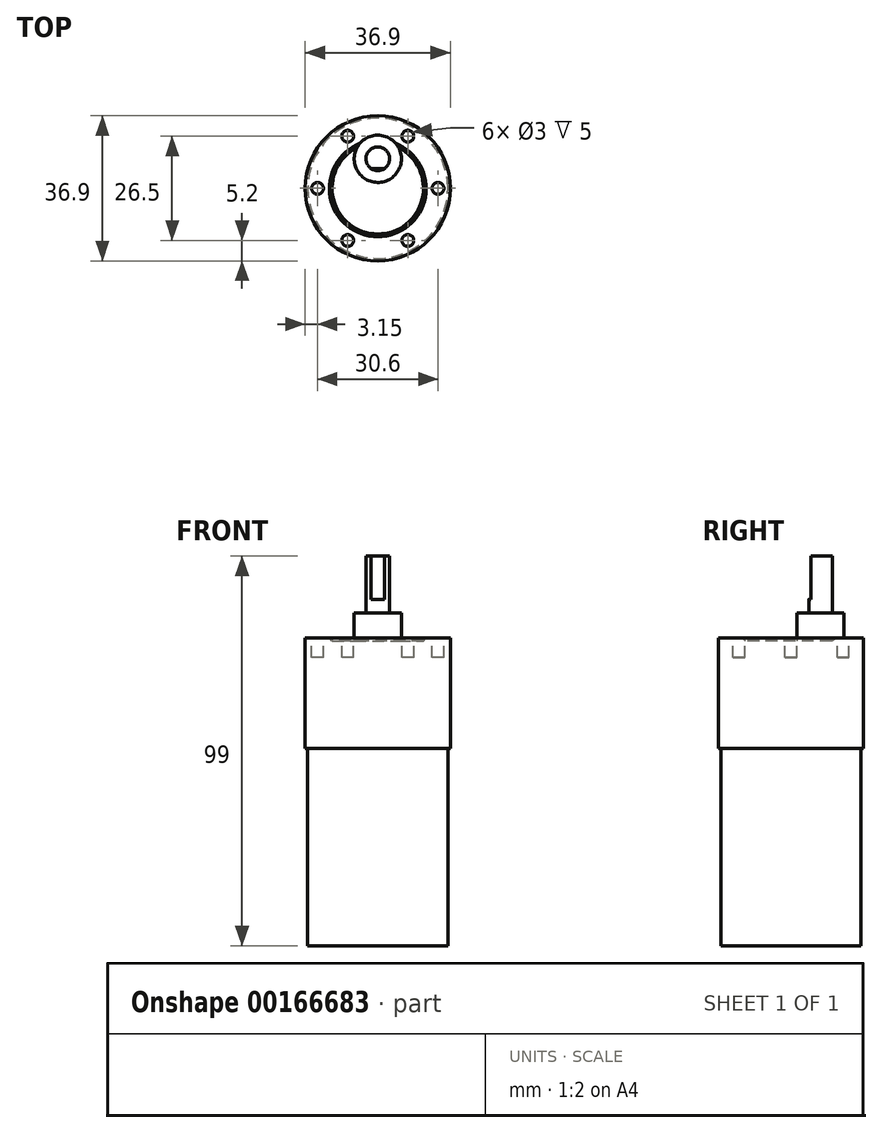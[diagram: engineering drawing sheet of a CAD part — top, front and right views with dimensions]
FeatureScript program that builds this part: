
annotation { "Feature Type Name" : "Feature", "Feature Type Description" : "" }
export const myFeature = defineFeature(function(context is Context, id is Id, definition is map)
    precondition{}
    {
        {
            var Q0;
            Q0=qCreatedBy(makeId("Right.planeOp"),FACE);
            var sketch = newSketch(context, id + "F0", { "sketchPlane" : qUnion([Q0])});
            skLineSegment(sketch, "E0", {"start": v(0, 0) * mm, "end": v(17.8, 0) * mm});
            skLineSegment(sketch, "E1", {"start": v(17.8, 0) * mm, "end": v(17.8, 50.2) * mm});
            skLineSegment(sketch, "E2", {"start": v(17.8, 50.2) * mm, "end": v(18.45, 50.2) * mm});
            skLineSegment(sketch, "E3", {"start": v(18.45, 50.2) * mm, "end": v(18.45, 78.2) * mm});
            skLineSegment(sketch, "E4", {"start": v(18.45, 78.2) * mm, "end": v(12.3, 78.2) * mm});
            skLineSegment(sketch, "E5", {"start": v(12.3, 78.2) * mm, "end": v(12.3, 77.5) * mm});
            skLineSegment(sketch, "E6", {"start": v(12.3, 77.5) * mm, "end": v(0, 77.5) * mm});
            skLineSegment(sketch, "E7", {"start": v(0, 77.5) * mm, "end": v(0, 0) * mm});
            skLineSegment(sketch, "E8", {"start": v(0, 71.31) * mm, "end": v(0, -59.15) * mm, "construction": true});
            skSolve(sketch);
        }
        {
            var Q0;
            Q0 = qSketchRegion(id + "F0", true);
            var Q1;
            Q1=sQuery(id+"F0.wireOp",EDGE,"E8");
            revolve(context, id + "F1", {"entities" : qUnion([Q0]), "axis" : qUnion([Q1]), "revolveType" : RevolveType.FULL});
        }
        {
            var Q0;
            Q0=makeQuery(id+"F1.opRevolve","SWEPT_FACE",FACE,{"disambiguationData":[OSD([sQuery(id+"F0.wireOp",EDGE,"E6")])]});
            var sketch = newSketch(context, id + "F2", { "sketchPlane" : qUnion([Q0])});
            skCircle(sketch, "E9", {"center": v(0, 7.5) * mm, "radius": 6 * mm});
            skSolve(sketch);
        }
        {
            var Q0;
            Q0 = qSketchRegion(id + "F2", true);
            extrude(context, id + "F3", {"entities" : qUnion([Q0]), "operationType" : NewBodyOperationType.ADD, "depth" : 7 * mm});
        }
        {
            var Q0;
            Q0=makeQuery(id+"F1.opRevolve","SWEPT_EDGE",EDGE,{"disambiguationData":[OSD([sQuery(id+"F0.wireOp",EDGE,"E5"),sQuery(id+"F0.wireOp",EDGE,"E6")])]});
            chamfer(context, id + "F4", {"entities" : qUnion([Q0]), "width" : 0.7 * mm, "tangentPropagation" : true});
        }
        {
            var Q0;
            Q0=makeQuery(id+"F1.opRevolve","SWEPT_FACE",FACE,{"disambiguationData":[OSD([sQuery(id+"F0.wireOp",EDGE,"E4")])]});
            var sketch = newSketch(context, id + "F5", { "sketchPlane" : qUnion([Q0])});
            skCircle(sketch, "E10", {"center": v(-15.3, 0) * mm, "radius": 1.5 * mm});
            skCircle(sketch, "E11.1.0", {"center": v(-7.65, -13.25) * mm, "radius": 1.5 * mm});
            skCircle(sketch, "E11.2.0", {"center": v(7.65, -13.25) * mm, "radius": 1.5 * mm});
            skCircle(sketch, "E11.3.0", {"center": v(15.3, 0) * mm, "radius": 1.5 * mm});
            skCircle(sketch, "E11.4.0", {"center": v(7.65, 13.25) * mm, "radius": 1.5 * mm});
            skCircle(sketch, "E11.5.0", {"center": v(-7.65, 13.25) * mm, "radius": 1.5 * mm});
            skPoint(sketch, "E11.center", {"position": v(0, 0) * mm});
            skSolve(sketch);
        }
        {
            var Q0;
            Q0 = qSketchRegion(id + "F5", true);
            extrude(context, id + "F6", {"entities" : qUnion([Q0]), "operationType" : NewBodyOperationType.REMOVE, "oppositeDirection" : true, "depth" : 5 * mm});
        }
        {
            var Q0;
            Q0=makeQuery(id+"F3.opExtrude","CAP_FACE",FACE,{"disambiguationData":[OSD([sQuery(id+"F2.wireOp",EDGE,"E9")])],"isStart":false});
            var sketch = newSketch(context, id + "F7", { "sketchPlane" : qUnion([Q0])});
            skArc(sketch, "E12", {"start": v(1.73, 5.05) * mm, "mid": v(0, 10.5) * mm, "end": v(-1.73, 5.05) * mm});
            skLineSegment(sketch, "E13", {"start": v(-1.73, 5.05) * mm, "end": v(1.73, 5.05) * mm});
            skSolve(sketch);
        }
        {
            var Q0;
            Q0 = qSketchRegion(id + "F7", true);
            extrude(context, id + "F8", {"entities" : qUnion([Q0]), "depth" : 14.5 * mm});
        }
        {
            var Q0;
            Q0=makeQuery(id+"F3.opExtrude","CAP_FACE",FACE,{"disambiguationData":[OSD([sQuery(id+"F2.wireOp",EDGE,"E9")])],"isStart":false});
            var sketch = newSketch(context, id + "F9", { "sketchPlane" : qUnion([Q0])});
            skCircle(sketch, "E14", {"center": v(0, 7.5) * mm, "radius": 3 * mm});
            skSolve(sketch);
        }
        {
            var Q0;
            Q0 = qSketchRegion(id + "F9", true);
            extrude(context, id + "F10", {"entities" : qUnion([Q0]), "operationType" : NewBodyOperationType.ADD, "depth" : 3.5 * mm});
        }
    });
